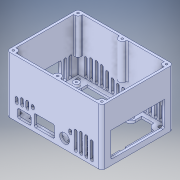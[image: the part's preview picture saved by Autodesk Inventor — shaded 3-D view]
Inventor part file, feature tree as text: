
AUTODESK INVENTOR PART (.ipt)
format: ipt  version: 2019 (Build 230136000, 136)  size: 551,936 bytes
history: native  units: in
note: dims shown in document units (in); Inventor stores cm internally (conversion verified against a paired STEP export)
features: sketch x4, extrude x3, direct_edit x2, move_body x2, other x1
ambient origin geometry x8: Origin, YZ Plane, XZ Plane, XY Plane, X Axis, Y Axis, Z Axis, Center Point
bodies: Solid1 (feature_tree)
feature tree (12):
  sketch  "Sketch1"  dims[d0=1.25in d1=0.0in d2=0.0in d3=0.0in d4=0.0in d5=1.25in]
  direct_edit  "Direct Edit1"
  direct_edit  "Direct Edit2"
  extrude  "Extrusion1"  Depth=1.25in TaperAngle=0.0deg
  extrude  "Extrusion2"  Depth=0.375in
  extrude  "Extrusion3"  Depth=1.0in
  sketch  "Sketch2"  dims[d6=2.25in d7=0.375in]
  sketch  "Sketch3"  dims[d8=1.0in d9=0.0in d12=0.25in]
  sketch  "Sketch4"  dims[d13=0.25in d14=0.25in d15=0.0in d16=0.25in d17=0.25in d18=0.0in d10=1.0in d11=1.0in d19=0.0625in d20=0.75in d21=0.375in]
  other  "Cut-Extrude12"
  move_body  "Move1"
  move_body  "Move2"
